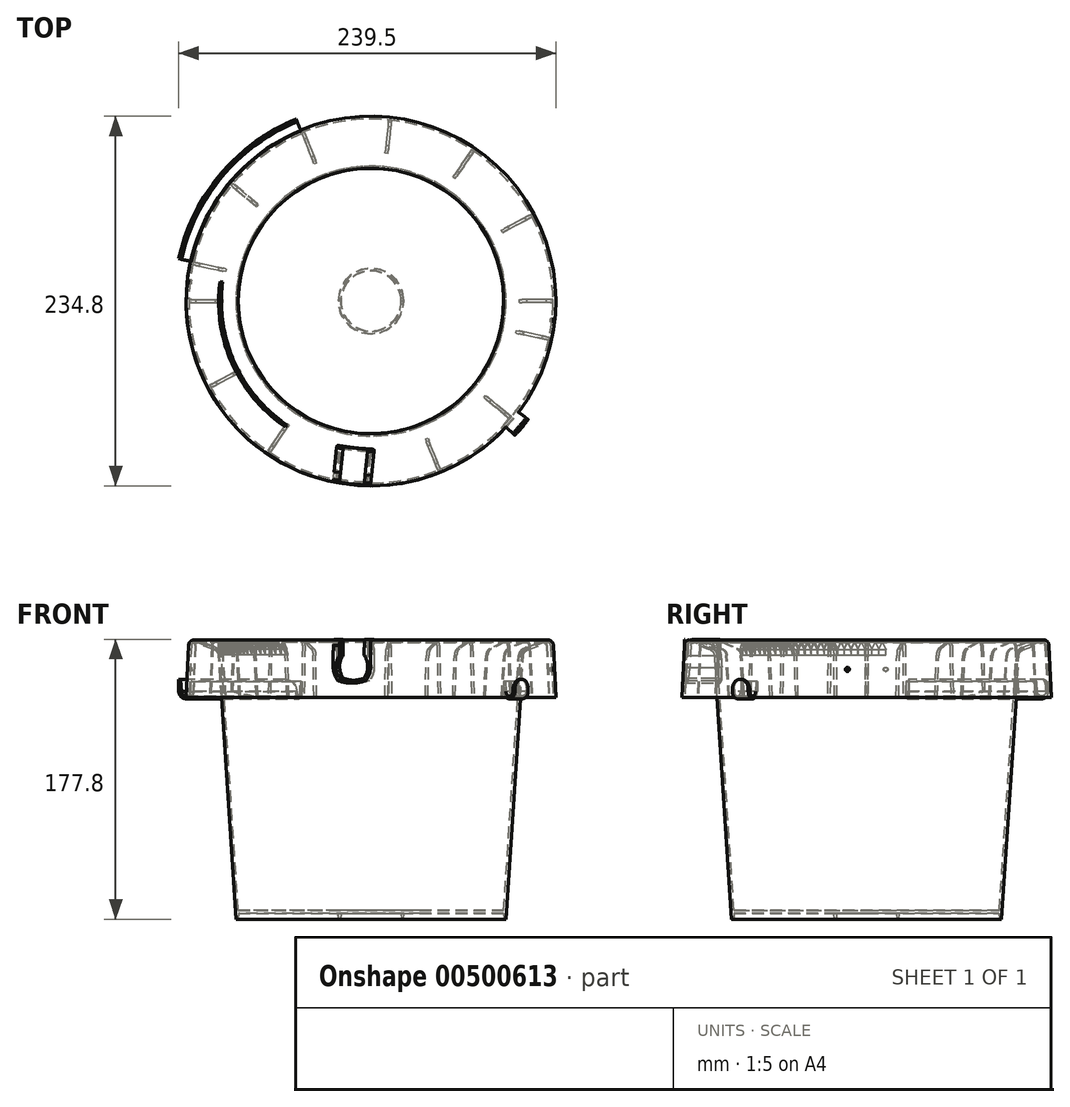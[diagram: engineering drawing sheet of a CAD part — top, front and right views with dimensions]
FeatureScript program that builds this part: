
annotation { "Feature Type Name" : "Feature", "Feature Type Description" : "" }
export const myFeature = defineFeature(function(context is Context, id is Id, definition is map)
    precondition{}
    {
        {
            var Q0;
            Q0=qCreatedBy(makeId("Front.planeOp"),FACE);
            var sketch = newSketch(context, id + "F0", { "sketchPlane" : qUnion([Q0])});
            skLineSegment(sketch, "E0", {"start": v(20.57, 0) * mm, "end": v(19.3, 0) * mm});
            skLineSegment(sketch, "E1", {"start": v(19.3, 0) * mm, "end": v(19.05, 3.81) * mm});
            skLineSegment(sketch, "E2", {"start": v(20.83, 3.81) * mm, "end": v(20.57, 0) * mm});
            skLineSegment(sketch, "E3", {"start": v(0, 0) * mm, "end": v(0, 3.81) * mm});
            skLineSegment(sketch, "E4", {"start": v(0, 3.81) * mm, "end": v(19.05, 3.81) * mm});
            skLineSegment(sketch, "E5", {"start": v(0, 3.81) * mm, "end": v(0, 5.59) * mm});
            skLineSegment(sketch, "E6", {"start": v(0, 5.59) * mm, "end": v(84.3, 5.59) * mm});
            skLineSegment(sketch, "E7", {"start": v(20.83, 3.81) * mm, "end": v(84.3, 3.8) * mm});
            skLineSegment(sketch, "E8", {"start": v(0, 0) * mm, "end": v(0, 179.07) * mm});
            skLineSegment(sketch, "E9", {"start": v(0, 0) * mm, "end": v(0, 171.45) * mm});
            skLineSegment(sketch, "E10", {"start": v(115.62, 140.97) * mm, "end": v(117.4, 140.97) * mm});
            skArc(sketch, "E11", {"start": v(114.08, 174) * mm, "mid": v(113.25, 175.47) * mm, "end": v(111.58, 175.66) * mm});
            skLineSegment(sketch, "E12", {"start": v(114.08, 174) * mm, "end": v(115.62, 140.97) * mm});
            skLineSegment(sketch, "E13", {"start": v(111.58, 175.66) * mm, "end": v(110.95, 177.32) * mm});
            skLineSegment(sketch, "E14", {"start": v(114.08, 174) * mm, "end": v(115.85, 174.1) * mm});
            skLineSegment(sketch, "E15", {"start": v(115.85, 174.1) * mm, "end": v(117.4, 140.97) * mm});
            skArc(sketch, "E16", {"start": v(99.32, 171.08) * mm, "mid": v(97.55, 169.74) * mm, "end": v(96.78, 167.65) * mm});
            skLineSegment(sketch, "E17", {"start": v(96.78, 167.65) * mm, "end": v(85.73, 0) * mm});
            skLineSegment(sketch, "E18", {"start": v(99.32, 171.08) * mm, "end": v(111.58, 175.66) * mm});
            skLineSegment(sketch, "E19", {"start": v(96.78, 167.65) * mm, "end": v(95, 167.77) * mm});
            skLineSegment(sketch, "E20", {"start": v(99.32, 171.08) * mm, "end": v(98.7, 172.74) * mm});
            skLineSegment(sketch, "E21", {"start": v(110.95, 177.32) * mm, "end": v(98.7, 172.74) * mm});
            skLineSegment(sketch, "E22", {"start": v(95, 167.77) * mm, "end": v(84.3, 5.59) * mm});
            skArc(sketch, "E23", {"start": v(98.7, 172.74) * mm, "mid": v(96.12, 170.8) * mm, "end": v(95, 167.77) * mm});
            skLineSegment(sketch, "E24", {"start": v(84.3, 3.8) * mm, "end": v(84.18, 3.8) * mm, "construction": true});
            skLineSegment(sketch, "E25", {"start": v(85.73, 0) * mm, "end": v(84.38, 0) * mm});
            skLineSegment(sketch, "E26", {"start": v(84.18, 3.8) * mm, "end": v(84.38, 0) * mm});
            skLineSegment(sketch, "E27", {"start": v(117.4, 140.97) * mm, "end": v(0, 140.97) * mm, "construction": true});
            skLineSegment(sketch, "E28", {"start": v(95, 167.77) * mm, "end": v(0, 167.77) * mm, "construction": true});
            skLineSegment(sketch, "E29", {"start": v(0, 177.32) * mm, "end": v(0, 179.1) * mm});
            skLineSegment(sketch, "E30", {"start": v(116.17, 167.13) * mm, "end": v(117.95, 167.13) * mm, "construction": true});
            skLineSegment(sketch, "E31", {"start": v(116.17, 167.13) * mm, "end": v(117.95, 167.13) * mm});
            skPoint(sketch, "E32.orphan", {"position": v(120.29, 167.13) * mm});
            skPoint(sketch, "E33.orphan", {"position": v(115.62, 167.13) * mm});
            skLineSegment(sketch, "E34", {"start": v(117.63, 174.1) * mm, "end": v(117.95, 167.13) * mm, "construction": true});
            skLineSegment(sketch, "E35", {"start": v(117.95, 167.13) * mm, "end": v(117.63, 174.1) * mm});
            skPoint(sketch, "E36.start.orphan", {"position": v(115.7, 177.55) * mm});
            skArc(sketch, "E37", {"start": v(117.63, 174.1) * mm, "mid": v(115.95, 177.7) * mm, "end": v(112.22, 179.07) * mm});
            skArc(sketch, "E38", {"start": v(115.85, 174.1) * mm, "mid": v(114.22, 176.95) * mm, "end": v(110.95, 177.32) * mm});
            skLineSegment(sketch, "E39", {"start": v(112.22, 177.55) * mm, "end": v(0, 177.55) * mm, "construction": true});
            skSolve(sketch);
        }
        {
            var Q0;
            Q0 = qSketchRegion(id + "F0", true);
            var Q1;
            Q1=sQuery(id+"F0.wireOp",EDGE,"E9");
            revolve(context, id + "F1", {"entities" : qUnion([Q0]), "axis" : qUnion([Q1]), "revolveType" : RevolveType.FULL});
        }
        {
            var Q0;
            Q0=qCreatedBy(makeId("Front.planeOp"),FACE);
            var sketch = newSketch(context, id + "F2", { "sketchPlane" : qUnion([Q0])});
            skLineSegment(sketch, "E40", {"start": v(0, 0) * mm, "end": v(0, 3.8) * mm});
            skLineSegment(sketch, "E41", {"start": v(0, 3.8) * mm, "end": v(0, 5.59) * mm});
            skLineSegment(sketch, "E42", {"start": v(0, 0) * mm, "end": v(0, 179.07) * mm});
            skLineSegment(sketch, "E43", {"start": v(0, 0) * mm, "end": v(0, 171.45) * mm});
            skLineSegment(sketch, "E44", {"start": v(0, 179.07) * mm, "end": v(157.98, 179.07) * mm, "construction": true});
            skLineSegment(sketch, "E45", {"start": v(0, 179.07) * mm, "end": v(115.62, 179.07) * mm, "construction": true});
            skLineSegment(sketch, "E46", {"start": v(114.08, 174.01) * mm, "end": v(115.62, 140.97) * mm});
            skLineSegment(sketch, "E47", {"start": v(0, 177.55) * mm, "end": v(129.4, 177.55) * mm, "construction": true});
            skLineSegment(sketch, "E48", {"start": v(111.31, 176.37) * mm, "end": v(99.06, 171.79) * mm});
            skLineSegment(sketch, "E49", {"start": v(94.26, 140.97) * mm, "end": v(96.02, 167.65) * mm});
            skArc(sketch, "E50", {"start": v(99.06, 171.79) * mm, "mid": v(96.93, 170.16) * mm, "end": v(96.02, 167.65) * mm});
            skArc(sketch, "E51", {"start": v(114.08, 174.01) * mm, "mid": v(113.2, 175.8) * mm, "end": v(111.31, 176.37) * mm});
            skLineSegment(sketch, "E52", {"start": v(115.62, 140.97) * mm, "end": v(94.26, 140.97) * mm});
            skSolve(sketch);
        }
        {
            var Q0;
            Q0=makeQuery(id+"F2.imprint","IMPRINT",FACE,{"disambiguationData":[TD([[makeQuery(id+"F2.imprint","IMPRINT",EDGE,{"derivedFrom":sQuery(id+"F2.wireOp",EDGE,"E46")}),-1.0]])]});
            extrude(context, id + "F3", {"entities" : qUnion([Q0]), "endBound" : BoundingType.SYMMETRIC, "depth" : 1.78 * mm});
        }
        {
            var Q0;
            Q0=makeQuery(id+"F3.opExtrude","SWEPT_BODY",BODY,{"disambiguationData":[OSD([sQuery(id+"F2.wireOp",EDGE,"E46"),sQuery(id+"F2.wireOp",EDGE,"E48"),sQuery(id+"F2.wireOp",EDGE,"E49"),sQuery(id+"F2.wireOp",EDGE,"E50"),sQuery(id+"F2.wireOp",EDGE,"E51"),sQuery(id+"F2.wireOp",EDGE,"E52")])]});
            var Q1;
            Q1=makeQuery(id+"F1.opRevolve","SWEPT_FACE",FACE,{"disambiguationData":[OSD([sQuery(id+"F0.wireOp",EDGE,"E15")])]});
            circularPattern(context, id + "F4", {"entities" : qUnion([Q0]), "axis" : qUnion([Q1]), "angle" : 12 * degree, "instanceCount" : 2, "equalSpace" : true});
        }
        {
            var Q0;
            Q0=makeQuery(id+"F3.opExtrude","SWEPT_BODY",BODY,{"disambiguationData":[OSD([sQuery(id+"F2.wireOp",EDGE,"E46"),sQuery(id+"F2.wireOp",EDGE,"E48"),sQuery(id+"F2.wireOp",EDGE,"E49"),sQuery(id+"F2.wireOp",EDGE,"E50"),sQuery(id+"F2.wireOp",EDGE,"E51"),sQuery(id+"F2.wireOp",EDGE,"E52")])]});
            var Q1;
            Q1=makeQuery(id+"F1.opRevolve","SWEPT_FACE",FACE,{"disambiguationData":[OSD([sQuery(id+"F0.wireOp",EDGE,"E12")])]});
            circularPattern(context, id + "F5", {"entities" : qUnion([Q0]), "axis" : qUnion([Q1]), "angle" : 28 * degree, "instanceCount" : 2, "equalSpace" : true});
        }
        {
            var Q0;
            Q0=makeQuery(id+"F3.opExtrude","SWEPT_BODY",BODY,{"disambiguationData":[OSD([sQuery(id+"F2.wireOp",EDGE,"E46"),sQuery(id+"F2.wireOp",EDGE,"E48"),sQuery(id+"F2.wireOp",EDGE,"E49"),sQuery(id+"F2.wireOp",EDGE,"E50"),sQuery(id+"F2.wireOp",EDGE,"E51"),sQuery(id+"F2.wireOp",EDGE,"E52")])]});
            var Q1;
            Q1=makeQuery(id+"F1.opRevolve","SWEPT_FACE",FACE,{"disambiguationData":[OSD([sQuery(id+"F0.wireOp",EDGE,"E12")])]});
            circularPattern(context, id + "F6", {"entities" : qUnion([Q0]), "axis" : qUnion([Q1]), "angle" : 56 * degree, "instanceCount" : 2, "equalSpace" : true});
        }
        {
            var Q0;
            Q0=makeQuery(id+"F3.opExtrude","SWEPT_BODY",BODY,{"disambiguationData":[OSD([sQuery(id+"F2.wireOp",EDGE,"E46"),sQuery(id+"F2.wireOp",EDGE,"E48"),sQuery(id+"F2.wireOp",EDGE,"E49"),sQuery(id+"F2.wireOp",EDGE,"E50"),sQuery(id+"F2.wireOp",EDGE,"E51"),sQuery(id+"F2.wireOp",EDGE,"E52")])]});
            var Q1;
            Q1=makeQuery(id+"F1.opRevolve","SWEPT_FACE",FACE,{"disambiguationData":[OSD([sQuery(id+"F0.wireOp",EDGE,"E12")])]});
            circularPattern(context, id + "F7", {"entities" : qUnion([Q0]), "axis" : qUnion([Q1]), "angle" : 84 * degree, "instanceCount" : 2, "equalSpace" : true});
        }
        {
            var Q0;
            Q0=makeQuery(id+"F1.opRevolve","SWEPT_BODY",BODY,{"disambiguationData":[OSD([sQuery(id+"F0.wireOp",EDGE,"E0"),sQuery(id+"F0.wireOp",EDGE,"E1"),sQuery(id+"F0.wireOp",EDGE,"E2"),sQuery(id+"F0.wireOp",EDGE,"E4"),sQuery(id+"F0.wireOp",EDGE,"E6"),sQuery(id+"F0.wireOp",EDGE,"E7"),sQuery(id+"F0.wireOp",EDGE,"E9"),sQuery(id+"F0.wireOp",EDGE,"E10"),sQuery(id+"F0.wireOp",EDGE,"E11"),sQuery(id+"F0.wireOp",EDGE,"E12"),sQuery(id+"F0.wireOp",EDGE,"E15"),sQuery(id+"F0.wireOp",EDGE,"LKbFe0pn-6IGS-4NvF-Y8YP-ZpA0iSk9hzCY"),sQuery(id+"F0.wireOp",EDGE,"E16"),sQuery(id+"F0.wireOp",EDGE,"E17"),sQuery(id+"F0.wireOp",EDGE,"E18"),sQuery(id+"F0.wireOp",EDGE,"E21"),sQuery(id+"F0.wireOp",EDGE,"E22"),sQuery(id+"F0.wireOp",EDGE,"E23"),sQuery(id+"F0.wireOp",EDGE,"E25"),sQuery(id+"F0.wireOp",EDGE,"E26")])]});
            var Q1;
            Q1=makeQuery(id+"F3.opExtrude","SWEPT_BODY",BODY,{"disambiguationData":[OSD([sQuery(id+"F2.wireOp",EDGE,"E46"),sQuery(id+"F2.wireOp",EDGE,"E48"),sQuery(id+"F2.wireOp",EDGE,"E49"),sQuery(id+"F2.wireOp",EDGE,"E50"),sQuery(id+"F2.wireOp",EDGE,"E51"),sQuery(id+"F2.wireOp",EDGE,"E52")])]});
            var Q2;
            Q2=makeQuery(id+"F1.opRevolve","SWEPT_FACE",FACE,{"disambiguationData":[OSD([sQuery(id+"F0.wireOp",EDGE,"E12")])]});
            circularPattern(context, id + "F8", {"entities" : qUnion([Q0, Q1]), "axis" : qUnion([Q2]), "angle" : 112 * degree, "instanceCount" : 2, "equalSpace" : true});
        }
        {
            var Q0;
            Q0=makeQuery(id+"F3.opExtrude","SWEPT_BODY",BODY,{"disambiguationData":[OSD([sQuery(id+"F2.wireOp",EDGE,"E46"),sQuery(id+"F2.wireOp",EDGE,"E48"),sQuery(id+"F2.wireOp",EDGE,"E49"),sQuery(id+"F2.wireOp",EDGE,"E50"),sQuery(id+"F2.wireOp",EDGE,"E51"),sQuery(id+"F2.wireOp",EDGE,"E52")])]});
            var Q1;
            Q1=makeQuery(id+"F8.opPattern","COPY",FACE,{"derivedFrom":makeQuery(id+"F1.opRevolve","SWEPT_FACE",FACE,{"disambiguationData":[OSD([sQuery(id+"F0.wireOp",EDGE,"E12")])]}),"instanceName":"1"});
            circularPattern(context, id + "F9", {"entities" : qUnion([Q0]), "axis" : qUnion([Q1]), "angle" : 140 * degree, "instanceCount" : 2, "equalSpace" : true});
        }
        {
            var Q0;
            Q0=makeQuery(id+"F3.opExtrude","SWEPT_BODY",BODY,{"disambiguationData":[OSD([sQuery(id+"F2.wireOp",EDGE,"E46"),sQuery(id+"F2.wireOp",EDGE,"E48"),sQuery(id+"F2.wireOp",EDGE,"E49"),sQuery(id+"F2.wireOp",EDGE,"E50"),sQuery(id+"F2.wireOp",EDGE,"E51"),sQuery(id+"F2.wireOp",EDGE,"E52")])]});
            var Q1;
            Q1=makeQuery(id+"F8.opPattern","COPY",FACE,{"derivedFrom":makeQuery(id+"F1.opRevolve","SWEPT_FACE",FACE,{"disambiguationData":[OSD([sQuery(id+"F0.wireOp",EDGE,"E12")])]}),"instanceName":"1"});
            circularPattern(context, id + "F10", {"entities" : qUnion([Q0]), "axis" : qUnion([Q1]), "angle" : 168 * degree, "instanceCount" : 2, "equalSpace" : true});
        }
        {
            var Q0;
            Q0=makeQuery(id+"F3.opExtrude","SWEPT_BODY",BODY,{"disambiguationData":[OSD([sQuery(id+"F2.wireOp",EDGE,"E46"),sQuery(id+"F2.wireOp",EDGE,"E48"),sQuery(id+"F2.wireOp",EDGE,"E49"),sQuery(id+"F2.wireOp",EDGE,"E50"),sQuery(id+"F2.wireOp",EDGE,"E51"),sQuery(id+"F2.wireOp",EDGE,"E52")])]});
            var Q1;
            Q1=makeQuery(id+"F1.opRevolve","SWEPT_FACE",FACE,{"disambiguationData":[OSD([sQuery(id+"F0.wireOp",EDGE,"E11")])]});
            circularPattern(context, id + "F11", {"entities" : qUnion([Q0]), "axis" : qUnion([Q1]), "angle" : 180 * degree, "instanceCount" : 2, "equalSpace" : true});
        }
        {
            var Q0;
            Q0=makeQuery(id+"F3.opExtrude","SWEPT_BODY",BODY,{"disambiguationData":[OSD([sQuery(id+"F2.wireOp",EDGE,"E46"),sQuery(id+"F2.wireOp",EDGE,"E48"),sQuery(id+"F2.wireOp",EDGE,"E49"),sQuery(id+"F2.wireOp",EDGE,"E50"),sQuery(id+"F2.wireOp",EDGE,"E51"),sQuery(id+"F2.wireOp",EDGE,"E52")])]});
            var Q1;
            Q1=makeQuery(id+"F8.opPattern","COPY",FACE,{"derivedFrom":makeQuery(id+"F1.opRevolve","SWEPT_FACE",FACE,{"disambiguationData":[OSD([sQuery(id+"F0.wireOp",EDGE,"E15")])]}),"instanceName":"1"});
            circularPattern(context, id + "F12", {"entities" : qUnion([Q0]), "axis" : qUnion([Q1]), "angle" : 208 * degree, "instanceCount" : 2, "oppositeDirection" : true, "equalSpace" : true});
        }
        {
            var Q0;
            Q0=makeQuery(id+"F3.opExtrude","SWEPT_BODY",BODY,{"disambiguationData":[OSD([sQuery(id+"F2.wireOp",EDGE,"E46"),sQuery(id+"F2.wireOp",EDGE,"E48"),sQuery(id+"F2.wireOp",EDGE,"E49"),sQuery(id+"F2.wireOp",EDGE,"E50"),sQuery(id+"F2.wireOp",EDGE,"E51"),sQuery(id+"F2.wireOp",EDGE,"E52")])]});
            var Q1;
            Q1=makeQuery(id+"F1.opRevolve","SWEPT_FACE",FACE,{"disambiguationData":[OSD([sQuery(id+"F0.wireOp",EDGE,"E15")])]});
            circularPattern(context, id + "F13", {"entities" : qUnion([Q0]), "axis" : qUnion([Q1]), "angle" : 236 * degree, "instanceCount" : 2, "oppositeDirection" : true, "equalSpace" : true});
        }
        {
            var Q0;
            Q0=makeQuery(id+"F3.opExtrude","SWEPT_BODY",BODY,{"disambiguationData":[OSD([sQuery(id+"F2.wireOp",EDGE,"E46"),sQuery(id+"F2.wireOp",EDGE,"E48"),sQuery(id+"F2.wireOp",EDGE,"E49"),sQuery(id+"F2.wireOp",EDGE,"E50"),sQuery(id+"F2.wireOp",EDGE,"E51"),sQuery(id+"F2.wireOp",EDGE,"E52")])]});
            var Q1;
            Q1=makeQuery(id+"F8.opPattern","COPY",FACE,{"derivedFrom":makeQuery(id+"F1.opRevolve","SWEPT_FACE",FACE,{"disambiguationData":[OSD([sQuery(id+"F0.wireOp",EDGE,"E12")])]}),"instanceName":"1"});
            circularPattern(context, id + "F14", {"entities" : qUnion([Q0]), "axis" : qUnion([Q1]), "angle" : 40 * degree, "instanceCount" : 2, "oppositeDirection" : true, "equalSpace" : true});
        }
        {
            var Q0;
            Q0=makeQuery(id+"F3.opExtrude","SWEPT_BODY",BODY,{"disambiguationData":[OSD([sQuery(id+"F2.wireOp",EDGE,"E46"),sQuery(id+"F2.wireOp",EDGE,"E48"),sQuery(id+"F2.wireOp",EDGE,"E49"),sQuery(id+"F2.wireOp",EDGE,"E50"),sQuery(id+"F2.wireOp",EDGE,"E51"),sQuery(id+"F2.wireOp",EDGE,"E52")])]});
            var Q1;
            Q1=makeQuery(id+"F1.opRevolve","SWEPT_FACE",FACE,{"disambiguationData":[OSD([sQuery(id+"F0.wireOp",EDGE,"E12")])]});
            circularPattern(context, id + "F15", {"entities" : qUnion([Q0]), "axis" : qUnion([Q1]), "angle" : 68 * degree, "instanceCount" : 2, "oppositeDirection" : true, "equalSpace" : true});
        }
        {
            var Q0;
            Q0=makeQuery(id+"F4.opPattern","COPY",FACE,{"derivedFrom":makeQuery(id+"F3.opExtrude","CAP_FACE",FACE,{"disambiguationData":[OSD([sQuery(id+"F2.wireOp",EDGE,"E46"),sQuery(id+"F2.wireOp",EDGE,"E48"),sQuery(id+"F2.wireOp",EDGE,"E49"),sQuery(id+"F2.wireOp",EDGE,"E50"),sQuery(id+"F2.wireOp",EDGE,"E51"),sQuery(id+"F2.wireOp",EDGE,"E52")])],"isStart":false}),"instanceName":"1"});
            var Q1;
            Q1=makeQuery(id+"F3.opExtrude","CAP_FACE",FACE,{"disambiguationData":[OSD([sQuery(id+"F2.wireOp",EDGE,"E46"),sQuery(id+"F2.wireOp",EDGE,"E48"),sQuery(id+"F2.wireOp",EDGE,"E49"),sQuery(id+"F2.wireOp",EDGE,"E50"),sQuery(id+"F2.wireOp",EDGE,"E51"),sQuery(id+"F2.wireOp",EDGE,"E52")])],"isStart":true});
            cPlane(context, id + "F16", {"entities" : qUnion([Q0, Q1]), "cplaneType" : CPlaneType.MID_PLANE, "offset" : 25.4 * mm, "width" : 152.4 * mm, "height" : 152.4 * mm});
        }
        {
            var Q0;
            Q0=qCreatedBy(id+"F16.planeOp",FACE);
            cPlane(context, id + "F17", {"entities" : qUnion([Q0]), "cplaneType" : CPlaneType.OFFSET, "offset" : 127 * mm, "width" : 152.4 * mm, "height" : 152.4 * mm});
        }
        {
            var Q0;
            Q0=makeQuery(id+"F7.opPattern","COPY",FACE,{"derivedFrom":makeQuery(id+"F3.opExtrude","CAP_FACE",FACE,{"disambiguationData":[OSD([sQuery(id+"F2.wireOp",EDGE,"E46"),sQuery(id+"F2.wireOp",EDGE,"E48"),sQuery(id+"F2.wireOp",EDGE,"E49"),sQuery(id+"F2.wireOp",EDGE,"E50"),sQuery(id+"F2.wireOp",EDGE,"E51"),sQuery(id+"F2.wireOp",EDGE,"E52")])],"isStart":false}),"instanceName":"1"});
            cPlane(context, id + "F18", {"entities" : qUnion([Q0]), "cplaneType" : CPlaneType.OFFSET, "offset" : 0.89 * mm, "oppositeDirection" : true, "width" : 152.4 * mm, "height" : 152.4 * mm});
        }
        {
            var Q0;
            Q0=qCreatedBy(id+"F18.planeOp",FACE);
            cPlane(context, id + "F19", {"entities" : qUnion([Q0]), "cplaneType" : CPlaneType.OFFSET, "offset" : 127 * mm, "width" : 152.4 * mm, "height" : 152.4 * mm});
        }
        {
            var Q0;
            Q0=qCreatedBy(id+"F19.planeOp",FACE);
            var sketch = newSketch(context, id + "F20", { "sketchPlane" : qUnion([Q0])});
            skLineSegment(sketch, "E53", {"start": v(0, 0) * mm, "end": v(0, 158.75) * mm, "construction": true});
            skCircle(sketch, "E54", {"center": v(0, 158.75) * mm, "radius": 1.27 * mm});
            skSolve(sketch);
        }
        {
            var Q0;
            Q0=makeQuery(id+"F20.imprint","IMPRINT",FACE,{"disambiguationData":[TD([[makeQuery(id+"F20.imprint","IMPRINT",EDGE,{"derivedFrom":sQuery(id+"F20.wireOp",EDGE,"E54")}),1.0]])]});
            extrude(context, id + "F21", {"entities" : qUnion([Q0]), "operationType" : NewBodyOperationType.REMOVE, "oppositeDirection" : true, "depth" : 25.4 * mm});
        }
        {
            var Q0;
            Q0=qCreatedBy(id+"F19.planeOp",FACE);
            cPlane(context, id + "F22", {"entities" : qUnion([Q0]), "cplaneType" : CPlaneType.OFFSET, "offset" : 254 * mm, "oppositeDirection" : true, "width" : 152.4 * mm, "height" : 152.4 * mm});
        }
        {
            var Q0;
            Q0=qCreatedBy(id+"F22.planeOp",FACE);
            var sketch = newSketch(context, id + "F23", { "sketchPlane" : qUnion([Q0])});
            skLineSegment(sketch, "E55", {"start": v(0, 0) * mm, "end": v(0, 158.75) * mm, "construction": true});
            skCircle(sketch, "E56", {"center": v(0, 158.75) * mm, "radius": 1.27 * mm});
            skSolve(sketch);
        }
        {
            var Q0;
            Q0=makeQuery(id+"F23.imprint","IMPRINT",FACE,{"disambiguationData":[TD([[makeQuery(id+"F23.imprint","IMPRINT",EDGE,{"derivedFrom":sQuery(id+"F23.wireOp",EDGE,"E56")}),1.0]])]});
            extrude(context, id + "F24", {"entities" : qUnion([Q0]), "operationType" : NewBodyOperationType.REMOVE, "depth" : 25.4 * mm});
        }
        {
            var Q0;
            Q0=qCreatedBy(id+"F17.planeOp",FACE);
            cPlane(context, id + "F25", {"entities" : qUnion([Q0]), "cplaneType" : CPlaneType.OFFSET, "offset" : 25.4 * mm, "oppositeDirection" : true, "width" : 152.4 * mm, "height" : 152.4 * mm});
        }
        {
            var Q0;
            Q0=qCreatedBy(id+"F16.planeOp",FACE);
            var sketch = newSketch(context, id + "F26", { "sketchPlane" : qUnion([Q0])});
            skLineSegment(sketch, "E57", {"start": v(0, 0) * mm, "end": v(-95, 0) * mm, "construction": true});
            skLineSegment(sketch, "E58", {"start": v(-95, 0) * mm, "end": v(-95, 167.77) * mm, "construction": true});
            skLineSegment(sketch, "E59", {"start": v(-95, 167.77) * mm, "end": v(-95, 176.02) * mm});
            skLineSegment(sketch, "E60", {"start": v(-95, 176.02) * mm, "end": v(-96.77, 176.02) * mm});
            skLineSegment(sketch, "E61", {"start": v(-96.77, 176.02) * mm, "end": v(-96.77, 171.3) * mm});
            skLineSegment(sketch, "E62", {"start": v(-95, 167.77) * mm, "end": v(-96.77, 171.3) * mm});
            skSolve(sketch);
        }
        {
            var Q0;
            Q0=makeQuery(id+"F26.imprint","IMPRINT",FACE,{"disambiguationData":[TD([[makeQuery(id+"F26.imprint","IMPRINT",EDGE,{"derivedFrom":sQuery(id+"F26.wireOp",EDGE,"E59")}),1.0]])]});
            extrude(context, id + "F27", {"entities" : qUnion([Q0]), "depth" : 2.22 * mm, "hasSecondDirection" : true, "secondDirectionOppositeDirection" : true, "secondDirectionDepth" : 2.22 * mm});
        }
        {
            var Q0;
            Q0=makeQuery(id+"F27.opExtrude","SWEPT_FACE",FACE,{"disambiguationData":[OSD([sQuery(id+"F26.wireOp",EDGE,"E61")])]});
            var sketch = newSketch(context, id + "F28", { "sketchPlane" : qUnion([Q0])});
            skLineSegment(sketch, "E63", {"start": v(2.22, 176.02) * mm, "end": v(2.22, 171.63) * mm});
            skLineSegment(sketch, "E64", {"start": v(2.22, 171.63) * mm, "end": v(0, 176.02) * mm});
            skLineSegment(sketch, "E65", {"start": v(0, 176.02) * mm, "end": v(2.22, 176.02) * mm});
            skSolve(sketch);
        }
        {
            var Q0;
            Q0=makeQuery(id+"F28.imprint","IMPRINT",FACE,{"disambiguationData":[TD([[makeQuery(id+"F28.imprint","IMPRINT",EDGE,{"derivedFrom":sQuery(id+"F28.wireOp",EDGE,"E63")}),-1.0]])]});
            extrude(context, id + "F29", {"entities" : qUnion([Q0]), "operationType" : NewBodyOperationType.REMOVE, "oppositeDirection" : true, "depth" : 25.4 * mm});
        }
        {
            var Q0;
            Q0=makeQuery(id+"F27.opExtrude","SWEPT_FACE",FACE,{"disambiguationData":[OSD([sQuery(id+"F26.wireOp",EDGE,"E61")])]});
            var sketch = newSketch(context, id + "F30", { "sketchPlane" : qUnion([Q0])});
            skLineSegment(sketch, "E66", {"start": v(0, 176.02) * mm, "end": v(-2.22, 176.02) * mm});
            skLineSegment(sketch, "E67", {"start": v(-2.22, 176.02) * mm, "end": v(-2.22, 171.64) * mm});
            skLineSegment(sketch, "E68", {"start": v(-2.22, 171.64) * mm, "end": v(0, 176.02) * mm});
            skSolve(sketch);
        }
        {
            var Q0;
            Q0=makeQuery(id+"F30.imprint","IMPRINT",FACE,{"disambiguationData":[TD([[makeQuery(id+"F30.imprint","IMPRINT",EDGE,{"derivedFrom":sQuery(id+"F30.wireOp",EDGE,"E66")}),1.0]])]});
            extrude(context, id + "F31", {"entities" : qUnion([Q0]), "operationType" : NewBodyOperationType.REMOVE, "oppositeDirection" : true, "depth" : 25.4 * mm});
        }
        {
            var Q0;
            Q0=makeQuery(id+"F27.opExtrude","SWEPT_BODY",BODY,{"disambiguationData":[OSD([sQuery(id+"F26.wireOp",EDGE,"E59"),sQuery(id+"F26.wireOp",EDGE,"E60"),sQuery(id+"F26.wireOp",EDGE,"E61"),sQuery(id+"F26.wireOp",EDGE,"E62")])]});
            var Q1;
            Q1=makeQuery(id+"F1.opRevolve","SWEPT_FACE",FACE,{"disambiguationData":[OSD([sQuery(id+"F0.wireOp",EDGE,"E22")])]});
            circularPattern(context, id + "F32", {"entities" : qUnion([Q0]), "axis" : qUnion([Q1]), "angle" : 60.5 * degree, "instanceCount" : 24, "oppositeDirection" : true, "equalSpace" : true});
        }
        {
            var Q0;
            Q0=makeQuery(id+"F10.opPattern","COPY",FACE,{"derivedFrom":makeQuery(id+"F3.opExtrude","CAP_FACE",FACE,{"disambiguationData":[OSD([sQuery(id+"F2.wireOp",EDGE,"E46"),sQuery(id+"F2.wireOp",EDGE,"E48"),sQuery(id+"F2.wireOp",EDGE,"E49"),sQuery(id+"F2.wireOp",EDGE,"E50"),sQuery(id+"F2.wireOp",EDGE,"E51"),sQuery(id+"F2.wireOp",EDGE,"E52")])],"isStart":false}),"instanceName":"1"});
            var sketch = newSketch(context, id + "F33", { "sketchPlane" : qUnion([Q0])});
            skLineSegment(sketch, "E69", {"start": v(115.5, 140.97) * mm, "end": v(115.05, 151.12) * mm});
            skLineSegment(sketch, "E70", {"start": v(117.3, 151.12) * mm, "end": v(118.28, 141.1) * mm});
            skLineSegment(sketch, "E71", {"start": v(117.3, 151.12) * mm, "end": v(115.05, 151.12) * mm});
            skLineSegment(sketch, "E72", {"start": v(118.28, 141.1) * mm, "end": v(118.46, 139.23) * mm});
            skLineSegment(sketch, "E73", {"start": v(115.5, 140.97) * mm, "end": v(115.5, 139.25) * mm});
            skLineSegment(sketch, "E74", {"start": v(115.5, 139.25) * mm, "end": v(118.46, 139.23) * mm});
            skSolve(sketch);
        }
        {
            var Q0;
            {var subQ2=sQuery(id+"F33.wireOp",EDGE,"E70");Q0=makeQuery(id+"F33.imprint","IMPRINT",FACE,{"disambiguationData":[TD([[makeQuery(id+"F33.imprint","IMPRINT",EDGE,{"derivedFrom":subQ2}),-1.0]])]});}
            var Q1;
            Q1=makeQuery(id+"F8.opPattern","COPY",FACE,{"derivedFrom":makeQuery(id+"F1.opRevolve","SWEPT_FACE",FACE,{"disambiguationData":[OSD([sQuery(id+"F0.wireOp",EDGE,"E15")])]}),"instanceName":"1"});
            revolve(context, id + "F34", {"operationType" : NewBodyOperationType.REMOVE, "entities" : qUnion([Q0]), "axis" : qUnion([Q1]), "revolveType" : RevolveType.ONE_DIRECTION, "angle" : 55 * degree});
        }
        {
            var Q0;
            {var subQ0=sQuery(id+"F33.wireOp",EDGE,"E71");Q0=makeQuery(id+"F34.boolean.opBoolean","COPY",FACE,{"disambiguationData":[TD([makeQuery(id+"F8.opPattern","COPY",FACE,{"derivedFrom":makeQuery(id+"F1.opRevolve","SWEPT_FACE",FACE,{"disambiguationData":[OSD([sQuery(id+"F0.wireOp",EDGE,"E10")])]}),"instanceName":"1"})])],"derivedFrom":makeQuery(id+"F34.opRevolve","CAP_FACE",FACE,{"disambiguationData":[OSD([sQuery(id+"F2.wireOp",EDGE,"E46"),sQuery(id+"F2.wireOp",EDGE,"E52"),sQuery(id+"F33.wireOp",EDGE,"E70"),subQ0,sQuery(id+"F33.wireOp",EDGE,"E72"),sQuery(id+"F33.wireOp",EDGE,"E73"),sQuery(id+"F33.wireOp",EDGE,"E74")])],"isStart":true})});}
            var sketch = newSketch(context, id + "F35", { "sketchPlane" : qUnion([Q0])});
            skLineSegment(sketch, "E75", {"start": v(115.62, 140.97) * mm, "end": v(125.02, 140.97) * mm, "construction": true});
            skLineSegment(sketch, "E76", {"start": v(115.62, 140.97) * mm, "end": v(120.32, 140.97) * mm, "construction": true});
            skLineSegment(sketch, "E77", {"start": v(116.92, 151.12) * mm, "end": v(115.15, 151.12) * mm});
            skLineSegment(sketch, "E78", {"start": v(115.15, 151.12) * mm, "end": v(115.44, 144.83) * mm});
            skLineSegment(sketch, "E79", {"start": v(115.44, 144.83) * mm, "end": v(115.44, 144.83) * mm});
            skArc(sketch, "E80", {"start": v(115.44, 144.83) * mm, "mid": v(120.23, 140.04) * mm, "end": v(125.02, 144.83) * mm});
            skLineSegment(sketch, "E81", {"start": v(125.02, 152.45) * mm, "end": v(123.75, 152.45) * mm});
            skLineSegment(sketch, "E82", {"start": v(123.75, 152.45) * mm, "end": v(123.24, 144.83) * mm});
            skLineSegment(sketch, "E83", {"start": v(120.23, 140.97) * mm, "end": v(120.23, 141.82) * mm});
            skArc(sketch, "E84", {"start": v(117.21, 144.83) * mm, "mid": v(120.23, 141.82) * mm, "end": v(123.24, 144.83) * mm});
            skLineSegment(sketch, "E85", {"start": v(116.92, 151.12) * mm, "end": v(117.21, 144.83) * mm});
            skPoint(sketch, "E86.orphan", {"position": v(120.23, 140.04) * mm});
            skLineSegment(sketch, "E87", {"start": v(125.02, 152.45) * mm, "end": v(125.02, 144.83) * mm});
            skLineSegment(sketch, "E88", {"start": v(0, 0) * mm, "end": v(0, 224.67) * mm, "construction": true});
            skLineSegment(sketch, "E89", {"start": v(115.44, 144.83) * mm, "end": v(0, 144.83) * mm, "construction": true});
            skLineSegment(sketch, "E90", {"start": v(0, 144.83) * mm, "end": v(0, 0) * mm, "construction": true});
            skLineSegment(sketch, "E91", {"start": v(0, 144.83) * mm, "end": v(0, 0) * mm});
            skSolve(sketch);
        }
        {
            var Q0;
            Q0=makeQuery(id+"F35.imprint","IMPRINT",FACE,{"disambiguationData":[TD([[makeQuery(id+"F35.imprint","IMPRINT",EDGE,{"derivedFrom":sQuery(id+"F35.wireOp",EDGE,"E81")}),1.0]])]});
            var Q1;
            Q1=makeQuery(id+"F35.imprint","IMPRINT",FACE,{"disambiguationData":[TD([[makeQuery(id+"F35.imprint","IMPRINT",EDGE,{"derivedFrom":sQuery(id+"F35.wireOp",EDGE,"E77")}),1.0]])]});
            var Q2;
            Q2=makeQuery(id+"F1.opRevolve","SWEPT_FACE",FACE,{"disambiguationData":[OSD([sQuery(id+"F0.wireOp",EDGE,"E15")])]});
            revolve(context, id + "F36", {"entities" : qUnion([Q0, Q1]), "axis" : qUnion([Q2]), "revolveType" : RevolveType.ONE_DIRECTION, "angle" : 55.2 * degree});
        }
        {
            var Q0;
            Q0=makeQuery(id+"F36.opRevolve","CAP_EDGE",EDGE,{"disambiguationData":[OSD([sQuery(id+"F35.wireOp",EDGE,"E81")]),OD(0.0)],"isStart":false});
            var Q1;
            Q1=makeQuery(id+"F36.opRevolve","CAP_EDGE",EDGE,{"disambiguationData":[OSD([sQuery(id+"F35.wireOp",EDGE,"E81")]),OD(1.0)],"isStart":false});
            fillet(context, id + "F37", {"entities" : qUnion([Q0, Q1]), "radius" : 7.62 * mm, "tangentPropagation" : true, "allowEdgeOverflow" : false});
        }
        {
            var Q0;
            Q0=makeQuery(id+"F9.opPattern","COPY",FACE,{"derivedFrom":makeQuery(id+"F3.opExtrude","CAP_FACE",FACE,{"disambiguationData":[OSD([sQuery(id+"F2.wireOp",EDGE,"E46"),sQuery(id+"F2.wireOp",EDGE,"E48"),sQuery(id+"F2.wireOp",EDGE,"E49"),sQuery(id+"F2.wireOp",EDGE,"E50"),sQuery(id+"F2.wireOp",EDGE,"E51"),sQuery(id+"F2.wireOp",EDGE,"E52")])],"isStart":true}),"instanceName":"1"});
            var sketch = newSketch(context, id + "F38", { "sketchPlane" : qUnion([Q0])});
            skLineSegment(sketch, "E92", {"start": v(-115.36, 144.6) * mm, "end": v(-115.62, 140.97) * mm});
            skLineSegment(sketch, "E93", {"start": v(-115.62, 140.97) * mm, "end": v(-94.98, 140.97) * mm});
            skLineSegment(sketch, "E94", {"start": v(-94.98, 140.97) * mm, "end": v(-115.36, 144.6) * mm});
            skSolve(sketch);
        }
        {
            var Q0;
            Q0=makeQuery(id+"F38.imprint","IMPRINT",FACE,{"disambiguationData":[TD([[makeQuery(id+"F38.imprint","IMPRINT",EDGE,{"derivedFrom":sQuery(id+"F38.wireOp",EDGE,"E92")}),1.0]])]});
            extrude(context, id + "F39", {"entities" : qUnion([Q0]), "operationType" : NewBodyOperationType.REMOVE, "oppositeDirection" : true, "depth" : 1.78 * mm});
        }
        {
            var Q0;
            Q0=makeQuery(id+"F9.opPattern","COPY",FACE,{"derivedFrom":makeQuery(id+"F3.opExtrude","CAP_FACE",FACE,{"disambiguationData":[OSD([sQuery(id+"F2.wireOp",EDGE,"E46"),sQuery(id+"F2.wireOp",EDGE,"E48"),sQuery(id+"F2.wireOp",EDGE,"E49"),sQuery(id+"F2.wireOp",EDGE,"E50"),sQuery(id+"F2.wireOp",EDGE,"E51"),sQuery(id+"F2.wireOp",EDGE,"E52")])],"isStart":true}),"instanceName":"1"});
            var sketch = newSketch(context, id + "F40", { "sketchPlane" : qUnion([Q0])});
            skLineSegment(sketch, "E95", {"start": v(-115.62, 140.97) * mm, "end": v(-115.36, 144.6) * mm});
            skLineSegment(sketch, "E96", {"start": v(-115.62, 140.97) * mm, "end": v(-115.45, 144.61) * mm});
            skLineSegment(sketch, "E97", {"start": v(-115.45, 144.61) * mm, "end": v(-115.36, 144.6) * mm});
            skSolve(sketch);
        }
        {
            var Q0;
            Q0=makeQuery(id+"F40.imprint","IMPRINT",FACE,{"disambiguationData":[TD([[makeQuery(id+"F40.imprint","IMPRINT",EDGE,{"derivedFrom":sQuery(id+"F40.wireOp",EDGE,"E95")}),-1.0]])]});
            extrude(context, id + "F41", {"entities" : qUnion([Q0]), "operationType" : NewBodyOperationType.REMOVE, "oppositeDirection" : true, "depth" : 1.78 * mm});
        }
        {
            var Q0;
            {var subQ0=sQuery(id+"F33.wireOp",EDGE,"E71");Q0=makeQuery(id+"F34.boolean.opBoolean","COPY",FACE,{"disambiguationData":[TD([makeQuery(id+"F8.opPattern","COPY",FACE,{"derivedFrom":makeQuery(id+"F1.opRevolve","SWEPT_FACE",FACE,{"disambiguationData":[OSD([sQuery(id+"F0.wireOp",EDGE,"E10")])]}),"instanceName":"1"})])],"derivedFrom":makeQuery(id+"F34.opRevolve","CAP_FACE",FACE,{"disambiguationData":[OSD([sQuery(id+"F2.wireOp",EDGE,"E46"),sQuery(id+"F2.wireOp",EDGE,"E52"),sQuery(id+"F33.wireOp",EDGE,"E70"),subQ0,sQuery(id+"F33.wireOp",EDGE,"E72"),sQuery(id+"F33.wireOp",EDGE,"E73"),sQuery(id+"F33.wireOp",EDGE,"E74")])],"isStart":false})});}
            var sketch = newSketch(context, id + "F42", { "sketchPlane" : qUnion([Q0])});
            skLineSegment(sketch, "E98", {"start": v(-115.62, 140.97) * mm, "end": v(-117.38, 140.97) * mm});
            skLineSegment(sketch, "E99", {"start": v(-115.62, 140.97) * mm, "end": v(-115.47, 144.2) * mm});
            skArc(sketch, "E100", {"start": v(-117.38, 140.97) * mm, "mid": v(-116.1, 142.39) * mm, "end": v(-115.47, 144.2) * mm});
            skSolve(sketch);
        }
        {
            var Q0;
            Q0=makeQuery(id+"F42.imprint","IMPRINT",FACE,{"disambiguationData":[TD([[makeQuery(id+"F42.imprint","IMPRINT",EDGE,{"derivedFrom":sQuery(id+"F42.wireOp",EDGE,"E98")}),1.0]])]});
            extrude(context, id + "F43", {"entities" : qUnion([Q0]), "operationType" : NewBodyOperationType.REMOVE, "oppositeDirection" : true, "depth" : 0.24 * mm});
        }
        {
            var Q0;
            Q0=qCreatedBy(id+"F25.planeOp",FACE);
            cPlane(context, id + "F44", {"entities" : qUnion([Q0]), "cplaneType" : CPlaneType.OFFSET, "offset" : 25.4 * mm, "width" : 152.4 * mm, "height" : 152.4 * mm});
        }
        {
            var Q0;
            Q0=qCreatedBy(id+"F44.planeOp",FACE);
            var sketch = newSketch(context, id + "F45", { "sketchPlane" : qUnion([Q0])});
            skLineSegment(sketch, "E101", {"start": v(0, 0) * mm, "end": v(0, 151.77) * mm, "construction": true});
            skLineSegment(sketch, "E102", {"start": v(-7.87, 177.8) * mm, "end": v(-7.87, 167.64) * mm});
            skLineSegment(sketch, "E103", {"start": v(7.87, 167.64) * mm, "end": v(7.87, 177.8) * mm});
            skArc(sketch, "E104", {"start": v(-7.87, 167.64) * mm, "mid": v(-10.16, 160.4) * mm, "end": v(-7.87, 153.16) * mm});
            skArc(sketch, "E105", {"start": v(7.87, 153.16) * mm, "mid": v(10.16, 160.4) * mm, "end": v(7.87, 167.64) * mm});
            skArc(sketch, "E106", {"start": v(-7.87, 153.16) * mm, "mid": v(0, 151.77) * mm, "end": v(7.87, 153.16) * mm});
            skPoint(sketch, "E107.orphan", {"position": v(0, 167.64) * mm});
            skLineSegment(sketch, "E108", {"start": v(-7.87, 177.8) * mm, "end": v(7.87, 177.8) * mm});
            skPoint(sketch, "E109.start.orphan", {"position": v(0, 160.4) * mm});
            skArc(sketch, "E110.2", {"start": v(9, 151.69) * mm, "mid": v(11.27, 156.07) * mm, "end": v(11.93, 160.97) * mm});
            skArc(sketch, "E110.4", {"start": v(-9, 151.69) * mm, "mid": v(0, 149.99) * mm, "end": v(9, 151.69) * mm});
            skArc(sketch, "E110.5", {"start": v(-11.93, 160.97) * mm, "mid": v(-11.27, 156.07) * mm, "end": v(-9, 151.69) * mm});
            skLineSegment(sketch, "E111", {"start": v(11.93, 159.83) * mm, "end": v(11.93, 177.8) * mm});
            skLineSegment(sketch, "E112", {"start": v(-11.93, 159.83) * mm, "end": v(-11.93, 177.8) * mm});
            skLineSegment(sketch, "E113", {"start": v(-7.87, 177.8) * mm, "end": v(-11.93, 177.8) * mm});
            skLineSegment(sketch, "E114", {"start": v(7.87, 177.8) * mm, "end": v(11.93, 177.8) * mm});
            skSolve(sketch);
        }
        {
            var Q0;
            Q0=makeQuery(id+"F45.imprint","IMPRINT",FACE,{"disambiguationData":[TD([[makeQuery(id+"F45.imprint","IMPRINT",EDGE,{"derivedFrom":sQuery(id+"F45.wireOp",EDGE,"E102")}),1.0]])]});
            var Q1;
            Q1=makeQuery(id+"F45.imprint","IMPRINT",FACE,{"disambiguationData":[TD([[makeQuery(id+"F45.imprint","IMPRINT",EDGE,{"derivedFrom":sQuery(id+"F45.wireOp",EDGE,"E102")}),-1.0]])]});
            extrude(context, id + "F46", {"entities" : qUnion([Q0, Q1]), "operationType" : NewBodyOperationType.REMOVE, "oppositeDirection" : true, "depth" : 50.8 * mm});
        }
        {
            var Q0;
            Q0=qCreatedBy(id+"F25.planeOp",FACE);
            var sketch = newSketch(context, id + "F47", { "sketchPlane" : qUnion([Q0])});
            skLineSegment(sketch, "E115", {"start": v(0, 0) * mm, "end": v(0, 151.77) * mm, "construction": true});
            skLineSegment(sketch, "E116", {"start": v(-7.87, 177.8) * mm, "end": v(-7.87, 167.64) * mm});
            skLineSegment(sketch, "E117", {"start": v(7.87, 167.64) * mm, "end": v(7.87, 177.8) * mm});
            skArc(sketch, "E118", {"start": v(-7.87, 167.64) * mm, "mid": v(-10.16, 160.4) * mm, "end": v(-7.87, 153.16) * mm});
            skArc(sketch, "E119", {"start": v(7.87, 153.16) * mm, "mid": v(10.16, 160.4) * mm, "end": v(7.87, 167.64) * mm});
            skArc(sketch, "E120", {"start": v(-7.87, 153.16) * mm, "mid": v(0, 151.77) * mm, "end": v(7.87, 153.16) * mm});
            skPoint(sketch, "E121.orphan", {"position": v(0, 167.64) * mm});
            skLineSegment(sketch, "E122", {"start": v(-7.87, 177.8) * mm, "end": v(7.87, 177.8) * mm});
            skPoint(sketch, "E123.start.orphan", {"position": v(0, 160.4) * mm});
            skArc(sketch, "E124.2", {"start": v(9, 151.69) * mm, "mid": v(11.27, 156.07) * mm, "end": v(11.93, 160.97) * mm});
            skArc(sketch, "E124.4", {"start": v(-9, 151.69) * mm, "mid": v(0, 149.99) * mm, "end": v(9, 151.69) * mm});
            skArc(sketch, "E124.5", {"start": v(-11.93, 160.97) * mm, "mid": v(-11.27, 156.07) * mm, "end": v(-9, 151.69) * mm});
            skLineSegment(sketch, "E125", {"start": v(11.93, 159.83) * mm, "end": v(11.93, 177.8) * mm});
            skLineSegment(sketch, "E126", {"start": v(-11.93, 159.83) * mm, "end": v(-11.93, 177.8) * mm});
            skLineSegment(sketch, "E127", {"start": v(-7.87, 177.8) * mm, "end": v(-11.93, 177.8) * mm});
            skLineSegment(sketch, "E128", {"start": v(7.87, 177.8) * mm, "end": v(11.93, 177.8) * mm});
            skSolve(sketch);
        }
        {
            var Q0;
            Q0=makeQuery(id+"F47.imprint","IMPRINT",FACE,{"disambiguationData":[TD([[makeQuery(id+"F47.imprint","IMPRINT",EDGE,{"derivedFrom":sQuery(id+"F47.wireOp",EDGE,"E116")}),-1.0]])]});
            var Q1;
            Q1=makeQuery(id+"F8.opPattern","COPY",FACE,{"derivedFrom":makeQuery(id+"F1.opRevolve","SWEPT_FACE",FACE,{"disambiguationData":[OSD([sQuery(id+"F0.wireOp",EDGE,"E15")])]}),"instanceName":"1"});
            var Q2;
            Q2=makeQuery(id+"F1.opRevolve","SWEPT_FACE",FACE,{"disambiguationData":[OSD([sQuery(id+"F0.wireOp",EDGE,"E22")])]});
            extrude(context, id + "F48", {"entities" : qUnion([Q0]), "endBound" : BoundingType.UP_TO_SURFACE, "endBoundEntityFace" : qUnion([Q1]), "depth" : 25.4 * mm, "hasSecondDirection" : true, "secondDirectionBound" : SecondDirectionBoundingType.UP_TO_SURFACE, "secondDirectionOppositeDirection" : true, "secondDirectionBoundEntityFace" : qUnion([Q2]), "secondDirectionDepth" : 25.4 * mm});
        }
        {
            var Q0;
            Q0=makeQuery(id+"F48.opExtrude","SWEPT_FACE",FACE,{"disambiguationData":[OSD([sQuery(id+"F47.wireOp",EDGE,"E125")])]});
            var sketch = newSketch(context, id + "F49", { "sketchPlane" : qUnion([Q0])});
            skLineSegment(sketch, "E129", {"start": v(-97.98, 172.74) * mm, "end": v(-110.32, 177.33) * mm});
            skLineSegment(sketch, "E130", {"start": v(-110.32, 177.33) * mm, "end": v(-90.5, 169.96) * mm});
            skLineSegment(sketch, "E131", {"start": v(-90.5, 169.96) * mm, "end": v(-118.42, 180.34) * mm});
            skLineSegment(sketch, "E132", {"start": v(-118.42, 180.34) * mm, "end": v(-116.7, 184.99) * mm});
            skLineSegment(sketch, "E133", {"start": v(-116.7, 184.99) * mm, "end": v(-94.35, 182.99) * mm});
            skLineSegment(sketch, "E134", {"start": v(-94.35, 182.99) * mm, "end": v(-90.5, 169.96) * mm});
            skSolve(sketch);
        }
        {
            var Q0;
            {var subQ0=sQuery(id+"F49.wireOp",EDGE,"E132");Q0=makeQuery(id+"F49.imprint","IMPRINT",FACE,{"disambiguationData":[TD([[makeQuery(id+"F49.imprint","IMPRINT",EDGE,{"derivedFrom":subQ0}),-1.0]])]});}
            var Q1;
            {var subQ0=sQuery(id+"F49.wireOp",EDGE,"E131");var subQ10=makeQuery(id+"F49.imprint","IMPRINT",VERTEX,{"disambiguationData":[OD(0.0)],"derivedFrom":subQ0});Q1=makeQuery(id+"F49.imprint","IMPRINT",FACE,{"disambiguationData":[TD([[makeQuery(id+"F49.imprint","IMPRINT",EDGE,{"disambiguationData":[TD([[subQ10,-1.0]])],"derivedFrom":subQ0}),-1.0]])]});}
            extrude(context, id + "F50", {"entities" : qUnion([Q0, Q1]), "operationType" : NewBodyOperationType.REMOVE, "oppositeDirection" : true, "depth" : 5.08 * mm});
        }
        {
            var Q0;
            Q0=makeQuery(id+"F48.opExtrude","SWEPT_FACE",FACE,{"disambiguationData":[OSD([sQuery(id+"F47.wireOp",EDGE,"E125")])]});
            var sketch = newSketch(context, id + "F51", { "sketchPlane" : qUnion([Q0])});
            skArc(sketch, "E135", {"start": v(-110.31, 177.32) * mm, "mid": v(-113.59, 176.96) * mm, "end": v(-115.23, 174.1) * mm});
            skLineSegment(sketch, "E136", {"start": v(-110.31, 177.32) * mm, "end": v(-109.66, 179.08) * mm});
            skLineSegment(sketch, "E137", {"start": v(-109.66, 179.08) * mm, "end": v(-117.53, 181.05) * mm});
            skLineSegment(sketch, "E138", {"start": v(-115.23, 174.1) * mm, "end": v(-117.42, 174.1) * mm});
            skLineSegment(sketch, "E139", {"start": v(-117.42, 174.1) * mm, "end": v(-117.53, 181.05) * mm});
            skSolve(sketch);
        }
        {
            var Q0;
            {var subQ1=sQuery(id+"F51.wireOp",EDGE,"E136");Q0=makeQuery(id+"F51.imprint","IMPRINT",FACE,{"disambiguationData":[TD([[makeQuery(id+"F51.imprint","IMPRINT",EDGE,{"derivedFrom":subQ1}),1.0]])]});}
            var Q1;
            {var subQ0=sQuery(id+"F51.wireOp",EDGE,"E135");var subQ1=makeQuery(id+"F50.boolean.opBoolean","COPY",EDGE,{"derivedFrom":makeQuery(id+"F50.opExtrude","CAP_EDGE",EDGE,{"disambiguationData":[OSD([sQuery(id+"F49.wireOp",EDGE,"E131")])],"isStart":true})});var subQ2=makeQuery(id+"F51.imprint","INTERSECT",VERTEX,{"derivedFrom":[subQ1,subQ0]});Q1=makeQuery(id+"F51.imprint","IMPRINT",FACE,{"disambiguationData":[TD([[makeQuery(id+"F51.imprint","IMPRINT",EDGE,{"disambiguationData":[TD([[subQ2,-1.0]])],"derivedFrom":subQ0}),-1.0]])]});}
            extrude(context, id + "F52", {"entities" : qUnion([Q0, Q1]), "operationType" : NewBodyOperationType.REMOVE, "oppositeDirection" : true, "depth" : 5.08 * mm});
        }
        {
            var Q0;
            Q0=makeQuery(id+"F48.opExtrude","SWEPT_FACE",FACE,{"disambiguationData":[OSD([sQuery(id+"F47.wireOp",EDGE,"E125")])]});
            var sketch = newSketch(context, id + "F53", { "sketchPlane" : qUnion([Q0])});
            skArc(sketch, "E140", {"start": v(-94.26, 167.77) * mm, "mid": v(-95.38, 170.8) * mm, "end": v(-97.98, 172.74) * mm});
            skLineSegment(sketch, "E141", {"start": v(-97.98, 172.74) * mm, "end": v(-96.3, 175.92) * mm});
            skLineSegment(sketch, "E142", {"start": v(-96.3, 175.92) * mm, "end": v(-88.68, 171.9) * mm});
            skLineSegment(sketch, "E143", {"start": v(-88.68, 171.9) * mm, "end": v(-92.08, 166.46) * mm});
            skLineSegment(sketch, "E144", {"start": v(-94.26, 167.77) * mm, "end": v(-92.5, 166.84) * mm});
            skLineSegment(sketch, "E145", {"start": v(-92.5, 166.84) * mm, "end": v(-92.08, 166.46) * mm});
            skSolve(sketch);
        }
        {
            var Q0;
            {var subQ0=sQuery(id+"F53.wireOp",EDGE,"E140");var subQ1=makeQuery(id+"F50.boolean.opBoolean","COPY",EDGE,{"derivedFrom":makeQuery(id+"F50.opExtrude","CAP_EDGE",EDGE,{"disambiguationData":[OSD([sQuery(id+"F49.wireOp",EDGE,"E131")])],"isStart":true})});var subQ2=makeQuery(id+"F53.imprint","INTERSECT",VERTEX,{"derivedFrom":[subQ1,subQ0]});Q0=makeQuery(id+"F53.imprint","IMPRINT",FACE,{"disambiguationData":[TD([[makeQuery(id+"F53.imprint","IMPRINT",EDGE,{"disambiguationData":[TD([[subQ2,1.0]])],"derivedFrom":subQ1}),1.0]])]});}
            var Q1;
            {var subQ0=sQuery(id+"F53.wireOp",EDGE,"E141");Q1=makeQuery(id+"F53.imprint","IMPRINT",FACE,{"disambiguationData":[TD([[makeQuery(id+"F53.imprint","IMPRINT",EDGE,{"derivedFrom":subQ0}),-1.0]])]});}
            extrude(context, id + "F54", {"entities" : qUnion([Q0, Q1]), "operationType" : NewBodyOperationType.REMOVE, "oppositeDirection" : true, "depth" : 5.08 * mm});
        }
        {
            var Q0;
            Q0=makeQuery(id+"F48.opExtrude","SWEPT_FACE",FACE,{"disambiguationData":[OSD([sQuery(id+"F47.wireOp",EDGE,"E126")])]});
            var sketch = newSketch(context, id + "F55", { "sketchPlane" : qUnion([Q0])});
            skLineSegment(sketch, "E146", {"start": v(110.32, 177.33) * mm, "end": v(97.98, 172.74) * mm});
            skLineSegment(sketch, "E147", {"start": v(97.98, 172.74) * mm, "end": v(120.99, 181.3) * mm});
            skLineSegment(sketch, "E148", {"start": v(120.99, 181.3) * mm, "end": v(87.56, 168.87) * mm});
            skLineSegment(sketch, "E149", {"start": v(87.56, 168.87) * mm, "end": v(87.36, 169.4) * mm});
            skLineSegment(sketch, "E150", {"start": v(87.36, 169.4) * mm, "end": v(87.56, 182.32) * mm});
            skLineSegment(sketch, "E151", {"start": v(87.56, 182.32) * mm, "end": v(120.99, 181.3) * mm});
            skSolve(sketch);
        }
        {
            var Q0;
            {var subQ0=sQuery(id+"F55.wireOp",EDGE,"E149");Q0=makeQuery(id+"F55.imprint","IMPRINT",FACE,{"disambiguationData":[TD([[makeQuery(id+"F55.imprint","IMPRINT",EDGE,{"derivedFrom":subQ0}),-1.0]])]});}
            var Q1;
            {var subQ0=sQuery(id+"F55.wireOp",EDGE,"E148");var subQ10=makeQuery(id+"F55.imprint","IMPRINT",VERTEX,{"disambiguationData":[OD(0.0)],"derivedFrom":subQ0});Q1=makeQuery(id+"F55.imprint","IMPRINT",FACE,{"disambiguationData":[TD([[makeQuery(id+"F55.imprint","IMPRINT",EDGE,{"disambiguationData":[TD([[subQ10,-1.0]])],"derivedFrom":subQ0}),-1.0]])]});}
            extrude(context, id + "F56", {"entities" : qUnion([Q0, Q1]), "operationType" : NewBodyOperationType.REMOVE, "oppositeDirection" : true, "depth" : 5.08 * mm});
        }
        {
            var Q0;
            Q0=makeQuery(id+"F48.opExtrude","SWEPT_FACE",FACE,{"disambiguationData":[OSD([sQuery(id+"F47.wireOp",EDGE,"E126")])]});
            var sketch = newSketch(context, id + "F57", { "sketchPlane" : qUnion([Q0])});
            skArc(sketch, "E152", {"start": v(115.23, 174.1) * mm, "mid": v(113.6, 176.95) * mm, "end": v(110.32, 177.33) * mm});
            skLineSegment(sketch, "E153", {"start": v(115.23, 174.1) * mm, "end": v(120.54, 174.1) * mm});
            skLineSegment(sketch, "E154", {"start": v(120.54, 174.1) * mm, "end": v(120.07, 180.05) * mm});
            skLineSegment(sketch, "E155", {"start": v(120.07, 180.05) * mm, "end": v(110.52, 180.05) * mm});
            skLineSegment(sketch, "E156", {"start": v(110.52, 180.05) * mm, "end": v(110.32, 177.33) * mm});
            skSolve(sketch);
        }
        {
            var Q0;
            {var subQ0=sQuery(id+"F57.wireOp",EDGE,"E152");var subQ1=makeQuery(id+"F56.boolean.opBoolean","COPY",EDGE,{"derivedFrom":makeQuery(id+"F56.opExtrude","CAP_EDGE",EDGE,{"disambiguationData":[OSD([sQuery(id+"F55.wireOp",EDGE,"E148")])],"isStart":true})});var subQ2=makeQuery(id+"F57.imprint","INTERSECT",VERTEX,{"derivedFrom":[subQ1,subQ0]});Q0=makeQuery(id+"F57.imprint","IMPRINT",FACE,{"disambiguationData":[TD([[makeQuery(id+"F57.imprint","IMPRINT",EDGE,{"disambiguationData":[TD([[subQ2,1.0]])],"derivedFrom":subQ0}),-1.0]])]});}
            var Q1;
            {var subQ0=sQuery(id+"F57.wireOp",EDGE,"E153");Q1=makeQuery(id+"F57.imprint","IMPRINT",FACE,{"disambiguationData":[TD([[makeQuery(id+"F57.imprint","IMPRINT",EDGE,{"derivedFrom":subQ0}),1.0]])]});}
            extrude(context, id + "F58", {"entities" : qUnion([Q0, Q1]), "operationType" : NewBodyOperationType.REMOVE, "oppositeDirection" : true, "depth" : 5.08 * mm});
        }
        {
            var Q0;
            Q0=makeQuery(id+"F48.opExtrude","SWEPT_FACE",FACE,{"disambiguationData":[OSD([sQuery(id+"F47.wireOp",EDGE,"E126")])]});
            var sketch = newSketch(context, id + "F59", { "sketchPlane" : qUnion([Q0])});
            skArc(sketch, "E157", {"start": v(97.98, 172.74) * mm, "mid": v(95.38, 170.8) * mm, "end": v(94.26, 167.77) * mm});
            skLineSegment(sketch, "E158", {"start": v(94.26, 167.77) * mm, "end": v(90.1, 167.77) * mm});
            skLineSegment(sketch, "E159", {"start": v(90.1, 167.77) * mm, "end": v(89.2, 176.46) * mm});
            skLineSegment(sketch, "E160", {"start": v(89.2, 176.46) * mm, "end": v(98.03, 178.16) * mm});
            skLineSegment(sketch, "E161", {"start": v(98.03, 178.16) * mm, "end": v(97.98, 172.74) * mm});
            skSolve(sketch);
        }
        {
            var Q0;
            {var subQ0=sQuery(id+"F59.wireOp",EDGE,"E157");var subQ1=makeQuery(id+"F56.boolean.opBoolean","COPY",EDGE,{"derivedFrom":makeQuery(id+"F56.opExtrude","CAP_EDGE",EDGE,{"disambiguationData":[OSD([sQuery(id+"F55.wireOp",EDGE,"E148")])],"isStart":true})});var subQ2=makeQuery(id+"F59.imprint","INTERSECT",VERTEX,{"derivedFrom":[subQ1,subQ0]});Q0=makeQuery(id+"F59.imprint","IMPRINT",FACE,{"disambiguationData":[TD([[makeQuery(id+"F59.imprint","IMPRINT",EDGE,{"disambiguationData":[TD([[subQ2,-1.0]])],"derivedFrom":subQ1}),1.0]])]});}
            var Q1;
            {var subQ0=sQuery(id+"F59.wireOp",EDGE,"E158");Q1=makeQuery(id+"F59.imprint","IMPRINT",FACE,{"disambiguationData":[TD([[makeQuery(id+"F59.imprint","IMPRINT",EDGE,{"derivedFrom":subQ0}),-1.0]])]});}
            extrude(context, id + "F60", {"entities" : qUnion([Q0, Q1]), "operationType" : NewBodyOperationType.REMOVE, "oppositeDirection" : true, "depth" : 5.08 * mm});
        }
        {
            var Q0;
            Q0=makeQuery(id+"F14.opPattern","COPY",FACE,{"derivedFrom":makeQuery(id+"F3.opExtrude","CAP_FACE",FACE,{"disambiguationData":[OSD([sQuery(id+"F2.wireOp",EDGE,"E46"),sQuery(id+"F2.wireOp",EDGE,"E48"),sQuery(id+"F2.wireOp",EDGE,"E49"),sQuery(id+"F2.wireOp",EDGE,"E50"),sQuery(id+"F2.wireOp",EDGE,"E51"),sQuery(id+"F2.wireOp",EDGE,"E52")])],"isStart":false}),"instanceName":"1"});
            cPlane(context, id + "F61", {"entities" : qUnion([Q0]), "cplaneType" : CPlaneType.OFFSET, "offset" : 0 * mm, "width" : 152.4 * mm, "height" : 152.4 * mm});
        }
        {
            var Q0;
            Q0=makeQuery(id+"F14.opPattern","COPY",FACE,{"derivedFrom":makeQuery(id+"F3.opExtrude","CAP_FACE",FACE,{"disambiguationData":[OSD([sQuery(id+"F2.wireOp",EDGE,"E46"),sQuery(id+"F2.wireOp",EDGE,"E48"),sQuery(id+"F2.wireOp",EDGE,"E49"),sQuery(id+"F2.wireOp",EDGE,"E50"),sQuery(id+"F2.wireOp",EDGE,"E51"),sQuery(id+"F2.wireOp",EDGE,"E52")])],"isStart":true}),"instanceName":"1"});
            cPlane(context, id + "F62", {"entities" : qUnion([Q0]), "cplaneType" : CPlaneType.OFFSET, "offset" : 0 * mm, "width" : 152.4 * mm, "height" : 152.4 * mm});
        }
        {
            var Q0;
            Q0=qCreatedBy(id+"F62.planeOp",FACE);
            var Q1;
            Q1=qCreatedBy(id+"F61.planeOp",FACE);
            cPlane(context, id + "F63", {"entities" : qUnion([Q0, Q1]), "cplaneType" : CPlaneType.MID_PLANE, "offset" : 25.4 * mm, "width" : 152.4 * mm, "height" : 152.4 * mm});
        }
        {
            var Q0;
            Q0=qCreatedBy(id+"F63.planeOp",FACE);
            var sketch = newSketch(context, id + "F64", { "sketchPlane" : qUnion([Q0])});
            skLineSegment(sketch, "E162", {"start": v(115.62, 140.97) * mm, "end": v(125.02, 140.97) * mm, "construction": true});
            skLineSegment(sketch, "E163", {"start": v(115.62, 140.97) * mm, "end": v(120.32, 140.97) * mm, "construction": true});
            skLineSegment(sketch, "E164", {"start": v(116.92, 151.12) * mm, "end": v(115.15, 151.12) * mm});
            skLineSegment(sketch, "E165", {"start": v(115.15, 151.12) * mm, "end": v(115.44, 144.83) * mm});
            skLineSegment(sketch, "E166", {"start": v(53.49, 211.36) * mm, "end": v(53.49, 211.36) * mm});
            skArc(sketch, "E167", {"start": v(115.44, 144.83) * mm, "mid": v(120.23, 140.04) * mm, "end": v(125.02, 144.83) * mm});
            skLineSegment(sketch, "E168", {"start": v(125.02, 152.45) * mm, "end": v(123.75, 152.45) * mm});
            skLineSegment(sketch, "E169", {"start": v(123.75, 152.45) * mm, "end": v(123.24, 144.83) * mm});
            skLineSegment(sketch, "E170", {"start": v(120.23, 140.97) * mm, "end": v(120.23, 141.82) * mm});
            skArc(sketch, "E171", {"start": v(117.22, 144.83) * mm, "mid": v(120.23, 141.82) * mm, "end": v(123.24, 144.83) * mm});
            skLineSegment(sketch, "E172", {"start": v(116.92, 151.12) * mm, "end": v(117.22, 144.83) * mm});
            skPoint(sketch, "E173.orphan", {"position": v(120.23, 140.04) * mm});
            skLineSegment(sketch, "E174", {"start": v(125.02, 152.45) * mm, "end": v(125.02, 144.83) * mm});
            skLineSegment(sketch, "E175", {"start": v(0, 0) * mm, "end": v(0, 224.67) * mm, "construction": true});
            skLineSegment(sketch, "E176", {"start": v(115.44, 144.83) * mm, "end": v(0, 144.83) * mm, "construction": true});
            skLineSegment(sketch, "E177", {"start": v(0, 144.83) * mm, "end": v(-115.44, 144.83) * mm, "construction": true});
            skLineSegment(sketch, "E178.MirrorCS", {"start": v(-115.15, 151.12) * mm, "end": v(-115.44, 144.83) * mm});
            skLineSegment(sketch, "E179.MirrorCS", {"start": v(-116.92, 151.12) * mm, "end": v(-115.15, 151.12) * mm});
            skLineSegment(sketch, "E180.MirrorCS", {"start": v(-116.92, 151.12) * mm, "end": v(-117.22, 144.83) * mm});
            skArc(sketch, "E181.MirrorCS", {"start": v(-117.22, 144.83) * mm, "mid": v(-120.23, 141.82) * mm, "end": v(-123.24, 144.83) * mm});
            skLineSegment(sketch, "E182.MirrorCS", {"start": v(-123.75, 152.45) * mm, "end": v(-123.24, 144.83) * mm});
            skLineSegment(sketch, "E183.MirrorCS", {"start": v(-125.02, 152.45) * mm, "end": v(-123.75, 152.45) * mm});
            skLineSegment(sketch, "E184.MirrorCS", {"start": v(-125.02, 152.45) * mm, "end": v(-125.02, 144.83) * mm});
            skArc(sketch, "E185.MirrorCS", {"start": v(-115.44, 144.83) * mm, "mid": v(-120.23, 140.04) * mm, "end": v(-125.02, 144.83) * mm});
            skLineSegment(sketch, "E186", {"start": v(0, 144.83) * mm, "end": v(0, 0) * mm, "construction": true});
            skSolve(sketch);
        }
        {
            var Q0;
            Q0=makeQuery(id+"F64.imprint","IMPRINT",FACE,{"disambiguationData":[TD([[makeQuery(id+"F64.imprint","IMPRINT",EDGE,{"derivedFrom":sQuery(id+"F64.wireOp",EDGE,"E178.MirrorCS")}),-1.0]])]});
            var Q1;
            Q1=sQuery(id+"F64.wireOp",EDGE,"E175");
            revolve(context, id + "F65", {"entities" : qUnion([Q0]), "axis" : qUnion([Q1]), "revolveType" : RevolveType.SYMMETRIC, "angle" : 6 * degree});
        }
        {
            var Q0;
            Q0=makeQuery(id+"F65.opRevolve","CAP_EDGE",EDGE,{"disambiguationData":[OSD([sQuery(id+"F64.wireOp",EDGE,"E183.MirrorCS")])],"isStart":true});
            var Q1;
            Q1=makeQuery(id+"F65.opRevolve","CAP_EDGE",EDGE,{"disambiguationData":[OSD([sQuery(id+"F64.wireOp",EDGE,"E183.MirrorCS")])],"isStart":false});
            fillet(context, id + "F66", {"entities" : qUnion([Q0, Q1]), "radius" : 6.35 * mm, "tangentPropagation" : true, "allowEdgeOverflow" : false});
        }
    });
